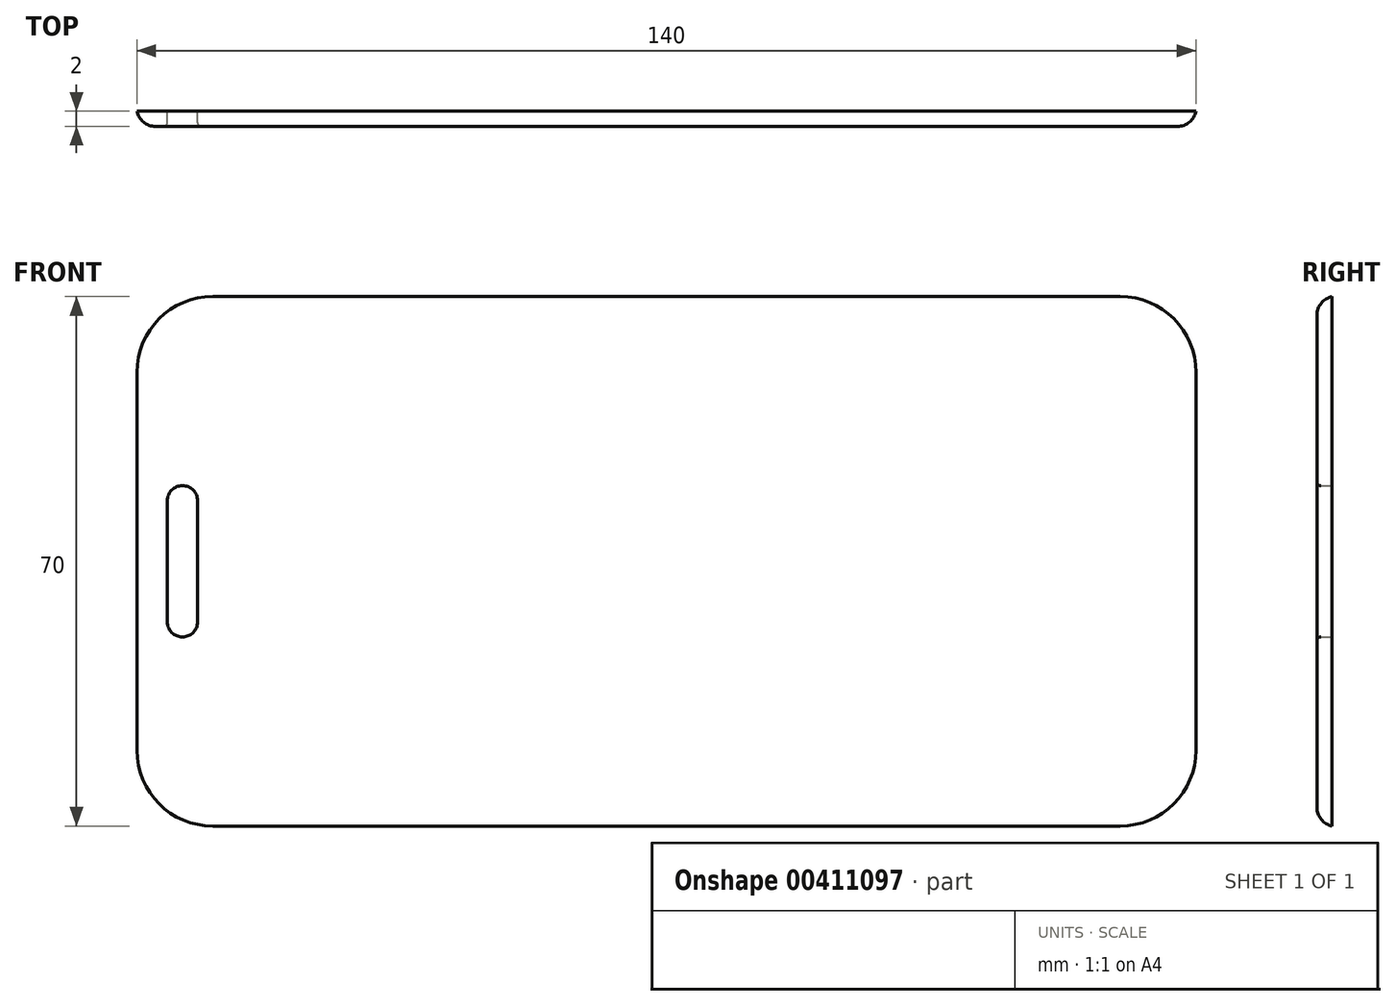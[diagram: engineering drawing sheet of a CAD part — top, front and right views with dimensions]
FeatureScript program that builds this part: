
annotation { "Feature Type Name" : "Feature", "Feature Type Description" : "" }
export const myFeature = defineFeature(function(context is Context, id is Id, definition is map)
    precondition{}
    {
        {
            var Q0;
            Q0=qCreatedBy(makeId("Front.planeOp"),FACE);
            var sketch = newSketch(context, id + "F0", { "sketchPlane" : qUnion([Q0])});
            skLineSegment(sketch, "E0.bottom", {"start": v(60, 35) * mm, "end": v(-60, 35) * mm});
            skLineSegment(sketch, "E0.top", {"start": v(60, -35) * mm, "end": v(-60, -35) * mm});
            skLineSegment(sketch, "E0.left", {"start": v(70, 25) * mm, "end": v(70, -25) * mm});
            skLineSegment(sketch, "E0.right", {"start": v(-70, 25) * mm, "end": v(-70, -25) * mm});
            skPoint(sketch, "E0.middle", {"position": v(0, 0) * mm});
            skPoint(sketch, "E1.visualSharp", {"position": v(-70, 35) * mm});
            skArc(sketch, "E1.filletArc", {"start": v(-60, 35) * mm, "mid": v(-67.07, 32.07) * mm, "end": v(-70, 25) * mm});
            skPoint(sketch, "E2.visualSharp", {"position": v(-70, -35) * mm});
            skArc(sketch, "E2.filletArc", {"start": v(-70, -25) * mm, "mid": v(-67.07, -32.07) * mm, "end": v(-60, -35) * mm});
            skPoint(sketch, "E3.visualSharp", {"position": v(70, -35) * mm});
            skArc(sketch, "E3.filletArc", {"start": v(60, -35) * mm, "mid": v(67.07, -32.07) * mm, "end": v(70, -25) * mm});
            skPoint(sketch, "E4.visualSharp", {"position": v(70, 35) * mm});
            skArc(sketch, "E4.filletArc", {"start": v(70, 25) * mm, "mid": v(67.07, 32.07) * mm, "end": v(60, 35) * mm});
            skSolve(sketch);
        }
        {
            var Q0;
            Q0 = qSketchRegion(id + "F0", true);
            extrude(context, id + "F1", {"entities" : qUnion([Q0]), "depth" : 2 * mm});
        }
        {
            var Q0;
            Q0=qCreatedBy(makeId("Front.planeOp"),FACE);
            var sketch = newSketch(context, id + "F2", { "sketchPlane" : qUnion([Q0])});
            skLineSegment(sketch, "E5.bottom", {"start": v(-64, 10) * mm, "end": v(-64, 10) * mm});
            skLineSegment(sketch, "E5.top", {"start": v(-64, -10) * mm, "end": v(-64, -10) * mm});
            skLineSegment(sketch, "E5.left", {"start": v(-62, 8) * mm, "end": v(-62, -8) * mm});
            skLineSegment(sketch, "E5.right", {"start": v(-66, 8) * mm, "end": v(-66, -8) * mm});
            skPoint(sketch, "E5.middle", {"position": v(-64, 0) * mm});
            skPoint(sketch, "E6.visualSharp", {"position": v(-62, 10) * mm});
            skArc(sketch, "E6.filletArc", {"start": v(-62, 8) * mm, "mid": v(-62.59, 9.41) * mm, "end": v(-64, 10) * mm});
            skPoint(sketch, "E7.visualSharp", {"position": v(-66, 10) * mm});
            skArc(sketch, "E7.filletArc", {"start": v(-64, 10) * mm, "mid": v(-65.41, 9.41) * mm, "end": v(-66, 8) * mm});
            skPoint(sketch, "E8.visualSharp", {"position": v(-66, -10) * mm});
            skArc(sketch, "E8.filletArc", {"start": v(-66, -8) * mm, "mid": v(-65.41, -9.41) * mm, "end": v(-64, -10) * mm});
            skPoint(sketch, "E9.visualSharp", {"position": v(-62, -10) * mm});
            skArc(sketch, "E9.filletArc", {"start": v(-64, -10) * mm, "mid": v(-62.59, -9.41) * mm, "end": v(-62, -8) * mm});
            skSolve(sketch);
        }
        {
            var Q0;
            Q0=makeQuery(id+"F2.imprint","IMPRINT",FACE,{"disambiguationData":[TD([[makeQuery(id+"F2.imprint","IMPRINT",EDGE,{"derivedFrom":sQuery(id+"F2.wireOp",EDGE,"E5.left")}),-1.0]])]});
            extrude(context, id + "F3", {"entities" : qUnion([Q0]), "operationType" : NewBodyOperationType.REMOVE, "depth" : 25 * mm});
        }
        {
            var Q0;
            Q0=makeQuery(id+"F1.opExtrude","CAP_EDGE",EDGE,{"disambiguationData":[OSD([sQuery(id+"F0.wireOp",EDGE,"E2.filletArc")])],"isStart":false});
            fillet(context, id + "F4", {"entities" : qUnion([Q0]), "radius" : 2.5 * mm, "tangentPropagation" : true, "allowEdgeOverflow" : false});
        }
        {
            var Q0;
            Q0=makeQuery(id+"F3.boolean.opBoolean","INTERSECT",EDGE,{"derivedFrom":[makeQuery(id+"F1.opExtrude","CAP_FACE",FACE,{"disambiguationData":[OSD([sQuery(id+"F0.wireOp",EDGE,"E0.bottom"),sQuery(id+"F0.wireOp",EDGE,"E0.top"),sQuery(id+"F0.wireOp",EDGE,"E0.left"),sQuery(id+"F0.wireOp",EDGE,"E0.right"),sQuery(id+"F0.wireOp",EDGE,"E1.filletArc"),sQuery(id+"F0.wireOp",EDGE,"E2.filletArc"),sQuery(id+"F0.wireOp",EDGE,"E3.filletArc"),sQuery(id+"F0.wireOp",EDGE,"E4.filletArc")])],"isStart":false}),makeQuery(id+"F3.opExtrude","SWEPT_FACE",FACE,{"disambiguationData":[OSD([sQuery(id+"F2.wireOp",EDGE,"E5.left")])]})]});
            var Q1;
            Q1=makeQuery(id+"F3.boolean.opBoolean","INTERSECT",EDGE,{"derivedFrom":[makeQuery(id+"F1.opExtrude","CAP_FACE",FACE,{"disambiguationData":[OSD([sQuery(id+"F0.wireOp",EDGE,"E0.bottom"),sQuery(id+"F0.wireOp",EDGE,"E0.top"),sQuery(id+"F0.wireOp",EDGE,"E0.left"),sQuery(id+"F0.wireOp",EDGE,"E0.right"),sQuery(id+"F0.wireOp",EDGE,"E1.filletArc"),sQuery(id+"F0.wireOp",EDGE,"E2.filletArc"),sQuery(id+"F0.wireOp",EDGE,"E3.filletArc"),sQuery(id+"F0.wireOp",EDGE,"E4.filletArc")])],"isStart":false}),makeQuery(id+"F3.opExtrude","SWEPT_FACE",FACE,{"disambiguationData":[OSD([sQuery(id+"F2.wireOp",EDGE,"E6.filletArc"),sQuery(id+"F2.wireOp",EDGE,"E7.filletArc")])]})]});
            var Q2;
            Q2=makeQuery(id+"F3.boolean.opBoolean","INTERSECT",EDGE,{"derivedFrom":[makeQuery(id+"F1.opExtrude","CAP_FACE",FACE,{"disambiguationData":[OSD([sQuery(id+"F0.wireOp",EDGE,"E0.bottom"),sQuery(id+"F0.wireOp",EDGE,"E0.top"),sQuery(id+"F0.wireOp",EDGE,"E0.left"),sQuery(id+"F0.wireOp",EDGE,"E0.right"),sQuery(id+"F0.wireOp",EDGE,"E1.filletArc"),sQuery(id+"F0.wireOp",EDGE,"E2.filletArc"),sQuery(id+"F0.wireOp",EDGE,"E3.filletArc"),sQuery(id+"F0.wireOp",EDGE,"E4.filletArc")])],"isStart":false}),makeQuery(id+"F3.opExtrude","SWEPT_FACE",FACE,{"disambiguationData":[OSD([sQuery(id+"F2.wireOp",EDGE,"E5.right")])]})]});
            var Q3;
            Q3=makeQuery(id+"F3.boolean.opBoolean","INTERSECT",EDGE,{"derivedFrom":[makeQuery(id+"F1.opExtrude","CAP_FACE",FACE,{"disambiguationData":[OSD([sQuery(id+"F0.wireOp",EDGE,"E0.bottom"),sQuery(id+"F0.wireOp",EDGE,"E0.top"),sQuery(id+"F0.wireOp",EDGE,"E0.left"),sQuery(id+"F0.wireOp",EDGE,"E0.right"),sQuery(id+"F0.wireOp",EDGE,"E1.filletArc"),sQuery(id+"F0.wireOp",EDGE,"E2.filletArc"),sQuery(id+"F0.wireOp",EDGE,"E3.filletArc"),sQuery(id+"F0.wireOp",EDGE,"E4.filletArc")])],"isStart":false}),makeQuery(id+"F3.opExtrude","SWEPT_FACE",FACE,{"disambiguationData":[OSD([sQuery(id+"F2.wireOp",EDGE,"E8.filletArc"),sQuery(id+"F2.wireOp",EDGE,"E9.filletArc")])]})]});
            fillet(context, id + "F5", {"entities" : qUnion([Q0, Q1, Q2, Q3]), "radius" : 0.5 * mm, "tangentPropagation" : true, "allowEdgeOverflow" : false});
        }
    });
